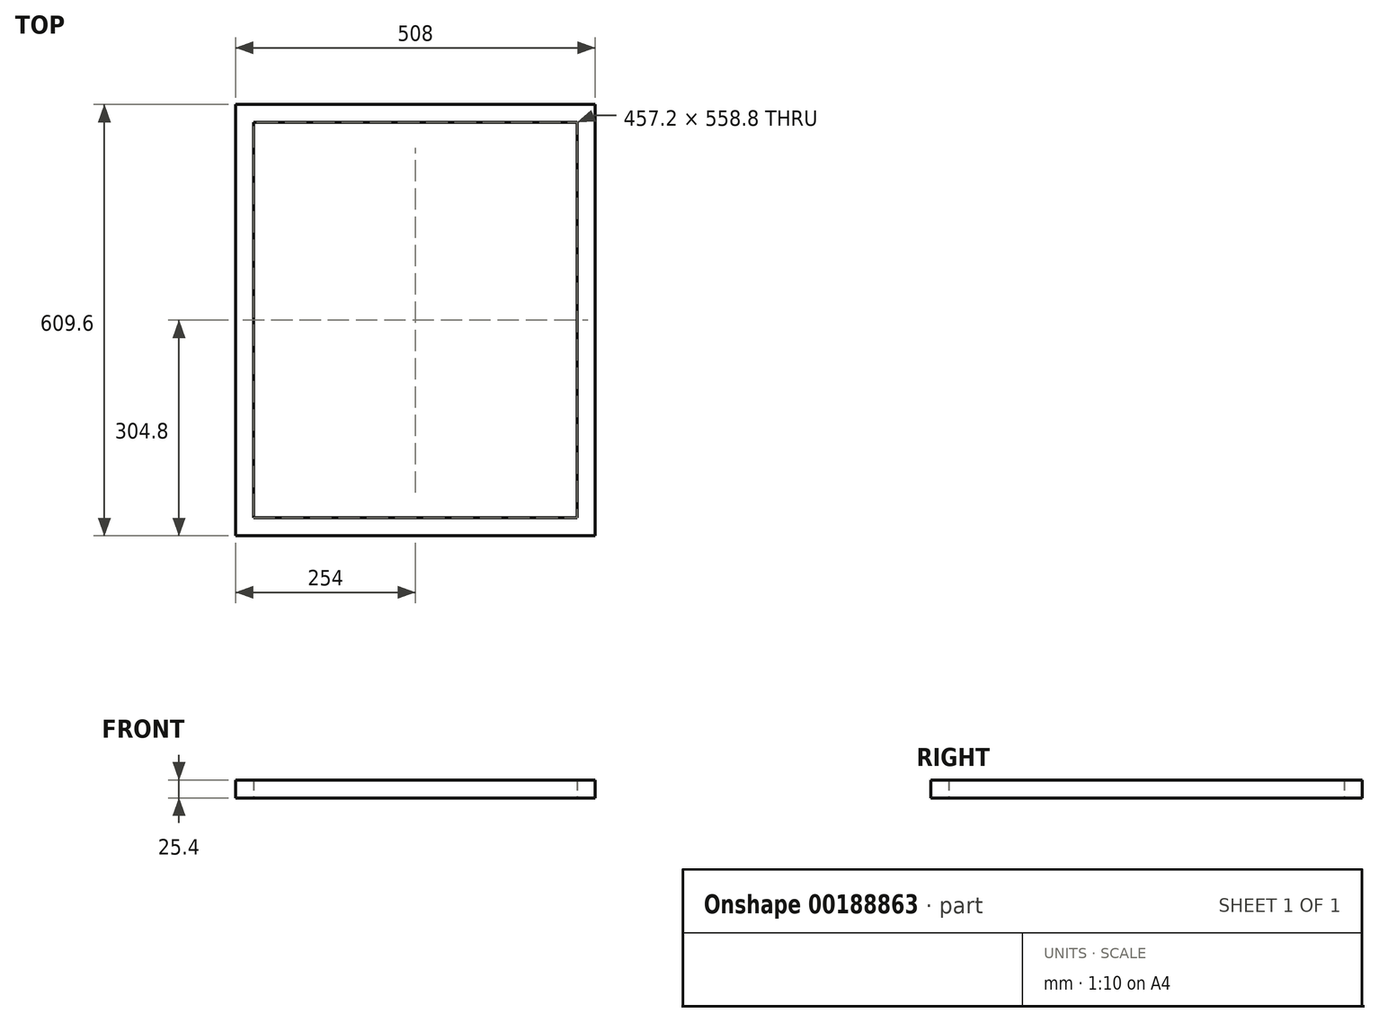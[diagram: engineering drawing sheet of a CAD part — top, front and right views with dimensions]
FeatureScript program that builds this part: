
annotation { "Feature Type Name" : "Feature", "Feature Type Description" : "" }
export const myFeature = defineFeature(function(context is Context, id is Id, definition is map)
    precondition{}
    {
        {
            var Q0;
            Q0=qCreatedBy(makeId("Top.planeOp"),FACE);
            var sketch = newSketch(context, id + "F0", { "sketchPlane" : qUnion([Q0])});
            skLineSegment(sketch, "E0.bottom", {"start": v(254, -304.8) * mm, "end": v(-254, -304.8) * mm});
            skLineSegment(sketch, "E0.top", {"start": v(254, 304.8) * mm, "end": v(-254, 304.8) * mm});
            skLineSegment(sketch, "E0.left", {"start": v(254, -304.8) * mm, "end": v(254, 304.8) * mm});
            skLineSegment(sketch, "E0.right", {"start": v(-254, -304.8) * mm, "end": v(-254, 304.8) * mm});
            skPoint(sketch, "E0.middle", {"position": v(0, 0) * mm});
            skLineSegment(sketch, "E1.bottom", {"start": v(228.6, -279.4) * mm, "end": v(-228.6, -279.4) * mm});
            skLineSegment(sketch, "E1.top", {"start": v(228.6, 279.4) * mm, "end": v(-228.6, 279.4) * mm});
            skLineSegment(sketch, "E1.left", {"start": v(228.6, -279.4) * mm, "end": v(228.6, 279.4) * mm});
            skLineSegment(sketch, "E1.right", {"start": v(-228.6, -279.4) * mm, "end": v(-228.6, 279.4) * mm});
            skSolve(sketch);
        }
        {
            var Q0;
            Q0=makeQuery(id+"F0.imprint","IMPRINT",FACE,{"disambiguationData":[TD([[makeQuery(id+"F0.imprint","IMPRINT",EDGE,{"derivedFrom":sQuery(id+"F0.wireOp",EDGE,"E0.bottom")}),-1.0]])]});
            var sketch = newSketch(context, id + "F1", { "sketchPlane" : qUnion([Q0])});
            skSolve(sketch);
        }
        {
            var Q0;
            Q0=makeQuery(id+"F1.imprint","IMPRINT",FACE,{"disambiguationData":[TD([[makeQuery(id+"F1.imprint","IMPRINT",EDGE,{"derivedFrom":makeQuery(id+"F0.imprint","IMPRINT",EDGE,{"derivedFrom":sQuery(id+"F0.wireOp",EDGE,"E0.bottom")})}),-1.0]])]});
            extrude(context, id + "F2", {"entities" : qUnion([Q0]), "depth" : 25.4 * mm, "offsetDistance" : 25.4 * mm});
        }
    });
